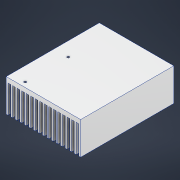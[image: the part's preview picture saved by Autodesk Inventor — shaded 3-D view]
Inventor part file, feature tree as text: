
AUTODESK INVENTOR PART (.ipt)
format: ipt  version: 2022 (Build 260153000, 153)  size: 189,952 bytes
history: native  units: in
note: dims shown in document units (in); Inventor stores cm internally (conversion verified against a paired STEP export)
features: sketch x2, extrude x1, hole x1
ambient origin geometry x8: Origin, YZ Plane, XZ Plane, XY Plane, X Axis, Y Axis, Z Axis, Center Point
bodies: Solid1 (feature_tree)
feature tree (4):
  extrude  "Extrusion1"  Depth=3.1496in
  hole  "Hole1"  [1 undecoded]
  sketch  "Sketch1"  dims[d0=1.378in d1=3.1496in]
  sketch  "Sketch2"  dims[d2=0.0787in d3=0.1969in d4=6.2992in d6=0.1919in d7=0.3937in d9=1.0in d11=0.0787in d12=0.0787in d13=3.937in d14=0.0in d15=1.82in d17=0.6in d18=0.203in d19=0.0968in d20=0.236in d21=0.375in d22=0.25in d23=0.5635in d24=1.0in d25=0.8108in]
note: 1 required parameter value undecoded (feature->parameter linkage not recoverable at this tier; creation-order binding heuristic only, values carry confidence <= 0.55)
